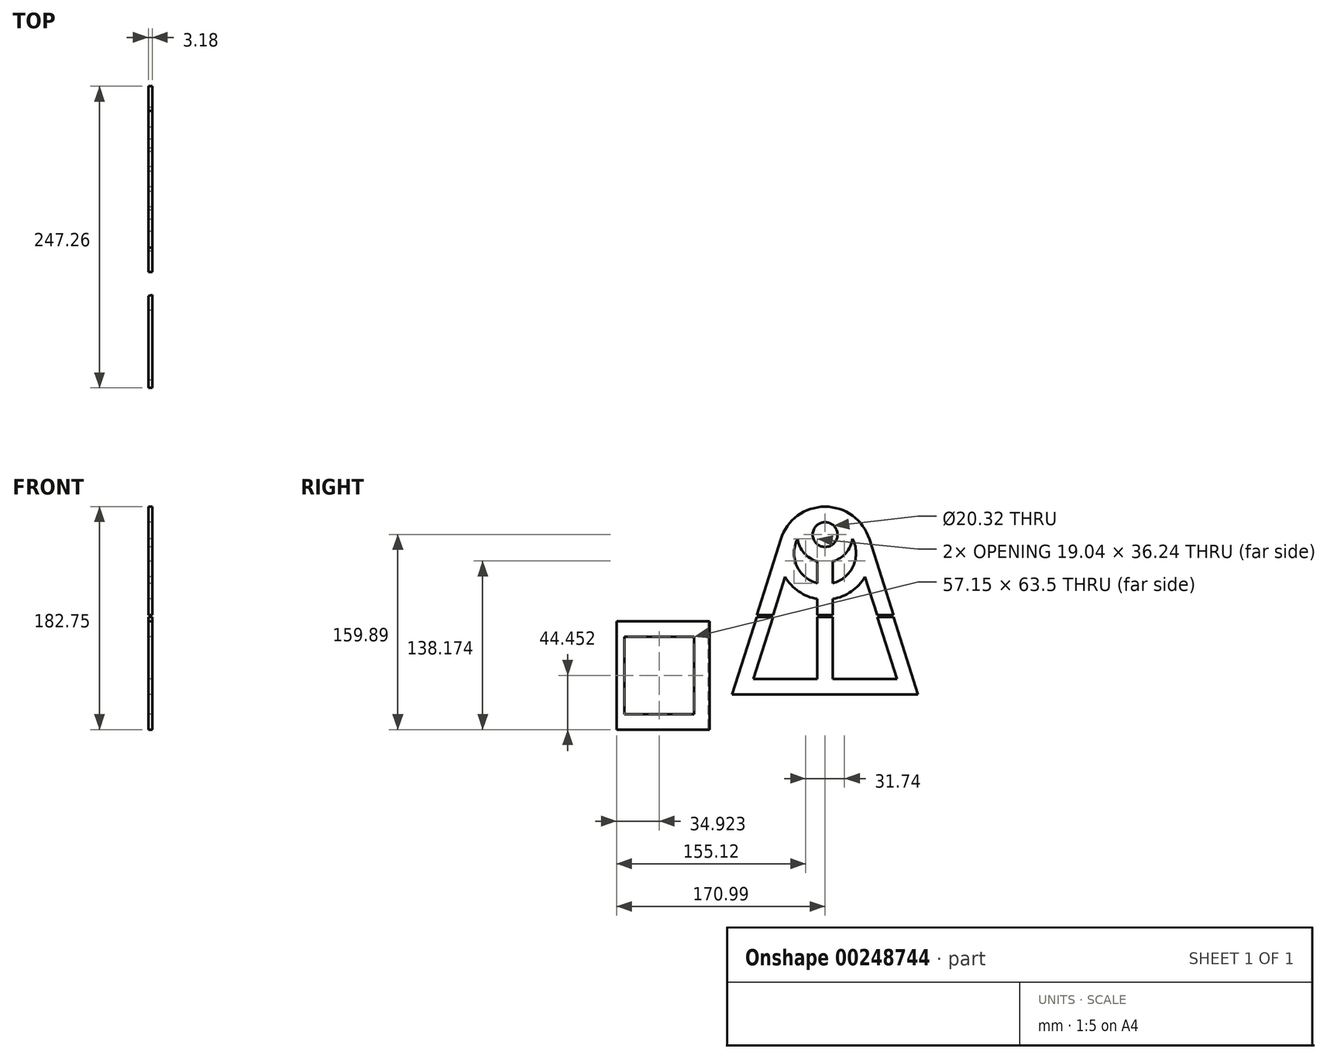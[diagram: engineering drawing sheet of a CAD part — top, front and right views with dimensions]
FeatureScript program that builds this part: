
annotation { "Feature Type Name" : "Feature", "Feature Type Description" : "" }
export const myFeature = defineFeature(function(context is Context, id is Id, definition is map)
    precondition{}
    {
        {
            var Q0;
            Q0=qCreatedBy(makeId("Right.planeOp"),FACE);
            var sketch = newSketch(context, id + "F0", { "sketchPlane" : qUnion([Q0])});
            skArc(sketch, "E0", {"start": v(36.32, 11.51) * mm, "mid": v(0, 38.1) * mm, "end": v(-36.32, 11.51) * mm});
            skLineSegment(sketch, "E1", {"start": v(-56.07, -50.8) * mm, "end": v(-36.32, 11.51) * mm});
            skLineSegment(sketch, "E2", {"start": v(36.32, 11.51) * mm, "end": v(56.07, -50.8) * mm});
            skLineSegment(sketch, "E3.1", {"start": v(-42.75, -50.8) * mm, "end": v(-32.8, -19.4) * mm});
            skLineSegment(sketch, "E3.2", {"start": v(32.8, -19.4) * mm, "end": v(42.75, -50.8) * mm});
            skArc(sketch, "E4.0", {"start": v(-32.8, -19.4) * mm, "mid": v(-21.58, -31.4) * mm, "end": v(-6.35, -37.57) * mm});
            skLineSegment(sketch, "E5", {"start": v(-6.35, -50.8) * mm, "end": v(-6.35, -37.57) * mm});
            skLineSegment(sketch, "E6", {"start": v(6.35, -50.8) * mm, "end": v(6.35, -37.57) * mm});
            skArc(sketch, "E7.trimOffspring", {"start": v(6.35, -37.57) * mm, "mid": v(21.58, -31.4) * mm, "end": v(32.8, -19.4) * mm});
            skLineSegment(sketch, "E8", {"start": v(0, 38.1) * mm, "end": v(0, -50.8) * mm});
            skLineSegment(sketch, "E9", {"start": v(56.07, -50.8) * mm, "end": v(42.75, -50.8) * mm});
            skLineSegment(sketch, "E10", {"start": v(-76.13, -116.01) * mm, "end": v(0.07, -116.01) * mm});
            skLineSegment(sketch, "E11", {"start": v(76.27, -116.01) * mm, "end": v(0.07, -116.01) * mm});
            skLineSegment(sketch, "E12", {"start": v(-76.13, -116.01) * mm, "end": v(-56, -52.51) * mm});
            skLineSegment(sketch, "E13", {"start": v(56.14, -52.51) * mm, "end": v(76.27, -116.01) * mm});
            skLineSegment(sketch, "E14.1", {"start": v(-58.79, -103.31) * mm, "end": v(-42.68, -52.51) * mm});
            skLineSegment(sketch, "E14.2", {"start": v(42.81, -52.51) * mm, "end": v(58.92, -103.31) * mm});
            skLineSegment(sketch, "E14.3", {"start": v(58.92, -103.31) * mm, "end": v(6.42, -103.31) * mm});
            skLineSegment(sketch, "E14.4", {"start": v(-58.79, -103.31) * mm, "end": v(-6.28, -103.31) * mm});
            skLineSegment(sketch, "E15", {"start": v(-6.28, -103.31) * mm, "end": v(-6.28, -52.51) * mm});
            skLineSegment(sketch, "E16", {"start": v(6.42, -103.31) * mm, "end": v(6.42, -52.51) * mm});
            skLineSegment(sketch, "E17", {"start": v(56.14, -52.51) * mm, "end": v(42.81, -52.51) * mm});
            skLineSegment(sketch, "E18.trimOffspring", {"start": v(-42.75, -50.8) * mm, "end": v(-56.07, -50.8) * mm});
            skLineSegment(sketch, "E19.trimOffspring", {"start": v(6.35, -50.8) * mm, "end": v(-6.35, -50.8) * mm});
            skPoint(sketch, "E20.orphan", {"position": v(66.69, -50.8) * mm});
            skLineSegment(sketch, "E21.trimOffspring", {"start": v(-42.68, -52.51) * mm, "end": v(-56, -52.51) * mm});
            skLineSegment(sketch, "E22.trimOffspring", {"start": v(6.42, -52.51) * mm, "end": v(-6.28, -52.51) * mm});
            skCircle(sketch, "E23", {"center": v(0, 15.24) * mm, "radius": 10.16 * mm});
            skArc(sketch, "E24", {"start": v(-22.58, 11.64) * mm, "mid": v(0, -7.62) * mm, "end": v(22.58, 11.64) * mm});
            skArc(sketch, "E25", {"start": v(-22.58, 11.64) * mm, "mid": v(0, -25.4) * mm, "end": v(22.58, 11.64) * mm});
            skLineSegment(sketch, "E26", {"start": v(-6.35, -24.6) * mm, "end": v(-6.35, -6.72) * mm});
            skLineSegment(sketch, "E27", {"start": v(6.35, -24.6) * mm, "end": v(6.35, -6.72) * mm});
            skArc(sketch, "E28", {"start": v(-37.5, -34.26) * mm, "mid": v(-23.37, -45.1) * mm, "end": v(-6.35, -50.4) * mm});
            skArc(sketch, "E29.trimOffspring", {"start": v(6.35, -50.4) * mm, "mid": v(23.37, -45.1) * mm, "end": v(37.5, -34.26) * mm});
            skLineSegment(sketch, "E30", {"start": v(-42.75, -50.8) * mm, "end": v(-6.35, -50.4) * mm});
            skLineSegment(sketch, "E31", {"start": v(6.35, -50.4) * mm, "end": v(42.75, -50.8) * mm});
            skSolve(sketch);
        }
        {
            var Q0;
            {var subQ10=sQuery(id+"F0.wireOp",EDGE,"E2");Q0=makeQuery(id+"F0.imprint","IMPRINT",FACE,{"disambiguationData":[TD([[makeQuery(id+"F0.imprint","IMPRINT",EDGE,{"derivedFrom":subQ10}),-1.0]])]});}
            var Q1;
            {var subQ14=sQuery(id+"F0.wireOp",EDGE,"E1");Q1=makeQuery(id+"F0.imprint","IMPRINT",FACE,{"disambiguationData":[TD([[makeQuery(id+"F0.imprint","IMPRINT",EDGE,{"derivedFrom":subQ14}),-1.0]])]});}
            var Q2;
            {var subQ5=sQuery(id+"F0.wireOp",EDGE,"E27");Q2=makeQuery(id+"F0.imprint","IMPRINT",FACE,{"disambiguationData":[TD([[makeQuery(id+"F0.imprint","IMPRINT",EDGE,{"derivedFrom":subQ5}),1.0]])]});}
            var Q3;
            {var subQ5=sQuery(id+"F0.wireOp",EDGE,"E26");Q3=makeQuery(id+"F0.imprint","IMPRINT",FACE,{"disambiguationData":[TD([[makeQuery(id+"F0.imprint","IMPRINT",EDGE,{"derivedFrom":subQ5}),-1.0]])]});}
            var Q4;
            Q4=makeQuery(id+"F0.imprint","IMPRINT",FACE,{"disambiguationData":[TD([[makeQuery(id+"F0.imprint","IMPRINT",EDGE,{"derivedFrom":sQuery(id+"F0.wireOp",EDGE,"E10")}),1.0]])]});
            extrude(context, id + "F1", {"entities" : qUnion([Q0, Q1, Q2, Q3, Q4]), "depth" : 3.17 * mm});
        }
        {
            var Q0;
            Q0=qCreatedBy(makeId("Right.planeOp"),FACE);
            var sketch = newSketch(context, id + "F2", { "sketchPlane" : qUnion([Q0])});
            skLineSegment(sketch, "E32.bottom", {"start": v(-94.8, -55.75) * mm, "end": v(-171, -55.75) * mm});
            skLineSegment(sketch, "E32.top", {"start": v(-94.8, -144.65) * mm, "end": v(-171, -144.65) * mm});
            skLineSegment(sketch, "E32.left", {"start": v(-94.8, -55.75) * mm, "end": v(-94.8, -144.65) * mm});
            skLineSegment(sketch, "E33.0", {"start": v(-107.5, -68.45) * mm, "end": v(-164.64, -68.45) * mm});
            skLineSegment(sketch, "E34.0", {"start": v(-107.5, -68.45) * mm, "end": v(-107.5, -131.95) * mm});
            skLineSegment(sketch, "E35.0", {"start": v(-107.5, -131.95) * mm, "end": v(-164.64, -131.95) * mm});
            skLineSegment(sketch, "E36", {"start": v(-171, -81.15) * mm, "end": v(-171, -131.95) * mm});
            skLineSegment(sketch, "E37", {"start": v(-164.64, -131.95) * mm, "end": v(-164.64, -68.45) * mm});
            skLineSegment(sketch, "E38", {"start": v(-171, -81.15) * mm, "end": v(-171, -55.75) * mm});
            skLineSegment(sketch, "E39", {"start": v(-171, -131.95) * mm, "end": v(-171, -144.65) * mm});
            skSolve(sketch);
        }
        {
            var Q0;
            Q0=makeQuery(id+"F2.imprint","IMPRINT",FACE,{"disambiguationData":[TD([[makeQuery(id+"F2.imprint","IMPRINT",EDGE,{"derivedFrom":sQuery(id+"F2.wireOp",EDGE,"E32.bottom")}),1.0]])]});
            extrude(context, id + "F3", {"entities" : qUnion([Q0]), "depth" : 3.17 * mm});
        }
        {
            var Q0;
            Q0=makeQuery(id+"F3.opExtrude","SWEPT_FACE",FACE,{"disambiguationData":[OSD([sQuery(id+"F2.wireOp",EDGE,"E32.top")])]});
            var sketch = newSketch(context, id + "F4", { "sketchPlane" : qUnion([Q0])});
            skLineSegment(sketch, "E40", {"start": v(3.18, 94.8) * mm, "end": v(-4.74, 97.3) * mm});
            skLineSegment(sketch, "E41", {"start": v(3.18, 94.8) * mm, "end": v(0, 94.8) * mm});
            skLineSegment(sketch, "E42", {"start": v(3.17, 94.8) * mm, "end": v(3.17, 103.99) * mm});
            skLineSegment(sketch, "E43", {"start": v(0, 94.8) * mm, "end": v(0, 95.8) * mm});
            skSolve(sketch);
        }
        {
            var Q0;
            {var subQ0=sQuery(id+"F4.wireOp",EDGE,"E41");Q0=makeQuery(id+"F4.imprint","IMPRINT",FACE,{"disambiguationData":[TD([[makeQuery(id+"F4.imprint","IMPRINT",EDGE,{"derivedFrom":subQ0}),-1.0]])]});}
            extrude(context, id + "F5", {"entities" : qUnion([Q0]), "operationType" : NewBodyOperationType.REMOVE, "oppositeDirection" : true, "depth" : 88.9 * mm});
        }
    });
